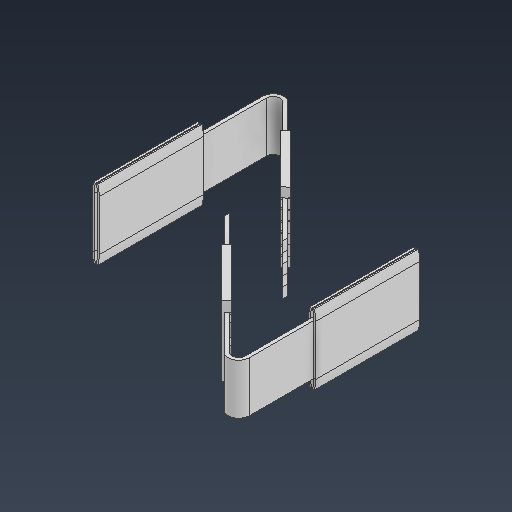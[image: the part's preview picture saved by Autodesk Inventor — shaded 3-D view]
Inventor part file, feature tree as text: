
AUTODESK INVENTOR PART (.ipt)
format: ipt  version: 2021 (Build 250183000, 183)  size: 491,520 bytes
history: native  units: mm
features: sketch x15, other x14, extrude x10, chamfer x1, pattern_circular x1
ambient origin geometry x8: Origin, YZ Plane, XZ Plane, XY Plane, X Axis, Y Axis, Z Axis, Center Point
bodies: Body1 (feature_tree)
feature tree (41):
  other  "Escovas"
  other  "Sólido1"
  extrude  "Extrusão1"  Depth=2.0mm TaperAngle=0.0deg
  sketch  "Esboço6"  dims[d31=45.0deg d32=1.0mm]
  extrude  "Extrusão6"  Depth=1.0mm
  extrude  "Extrusão7"  Depth=0.15mm
  extrude  "Extrusão8"  Depth=0.2mm
  extrude  "Extrusão9"  Depth=0.2mm
  extrude  "Extrusão10"  Depth=2.0mm
  extrude  "Extrusão11"  Depth=1.5mm
  chamfer  "Chanfro1"  Distance=1.5mm
  extrude  "Extrusão12"  Depth=0.275mm TaperAngle=0.0deg
  other  "Vergar peça1"
  other  "Vergar peça2"
  extrude  "Extrusão13"  Depth=0.275mm TaperAngle=0.0deg
  other  "Vergar peça3"
  other  "Vergar peça4"
  extrude  "Extrusão14"  Depth=2.0mm
  pattern_circular  "Padrão circular2"  [2 undecoded]
  sketch  "Esboço1"  dims[d0=45.0deg d9=2.0mm d10=0.0mm]
  sketch  "Esboço7"  dims[d34=45.0deg d35=0.15mm]
  sketch  "Esboço8"  dims[d36=45.0deg d37=0.2mm]
  other  "Contorno projetado4"
  sketch  "Esboço9"  dims[d38=0.35mm d39=0.2mm]
  other  "Contorno projetado5"
  sketch  "Esboço10"  dims[d40=2.0mm d41=2.0mm]
  sketch  "Esboço11"  dims[d42=1.5mm d43=0.4mm]
  other  "Contorno projetado6"
  other  "Contorno projetado7"
  other  "Contorno projetado8"
  sketch  "Esboço12"  dims[d44=2.0mm]
  other  "Contorno projetado9"
  sketch  "Esboço13"  dims[d45=0.3mm]
  sketch  "Esboço14"  dims[d46=0.275mm]
  sketch  "Esboço15"  dims[d47=0.3mm]
  sketch  "Esboço16"  dims[d48=0.275mm]
  other  "Contorno projetado10"
  other  "Contorno projetado11"
  sketch  "Esboço17"  dims[d49=0.3mm]
  sketch  "Esboço18"  dims[d50=0.275mm d51=1.5mm d52=0.0mm]
  sketch  "Esboço19"  dims[d53=3.0mm d54=0.275mm d55=0.0mm d56=0.275mm d57=0.0mm d58=2.0mm d59=2.0mm d60=2.0mm d61=0.05mm d62=0.0mm d63=0.05mm d64=0.0mm d65=2.0mm d66=0.0mm d67=0.1mm d68=2.0mm d69=45.0deg d70=0.1mm d71=0.275mm d72=0.0mm d73=1.0mm d74=45.0deg d75=1.0mm d76=45.0deg d77=0.275mm d78=0.0mm d79=1.0mm d80=45.0deg d81=1.0mm d82=45.0deg d83=0.275mm d84=0.0mm d88=0.05mm d89=0.05mm d90=2.0mm d91=0.05mm d92=0.05mm d93=0.05mm d94=0.05mm d95=20.0mm d96=360.0deg d11=0.5mm d12=0.872665mm]
note: 2 required parameter values undecoded (feature->parameter linkage not recoverable at this tier; creation-order binding heuristic only, values carry confidence <= 0.55)
